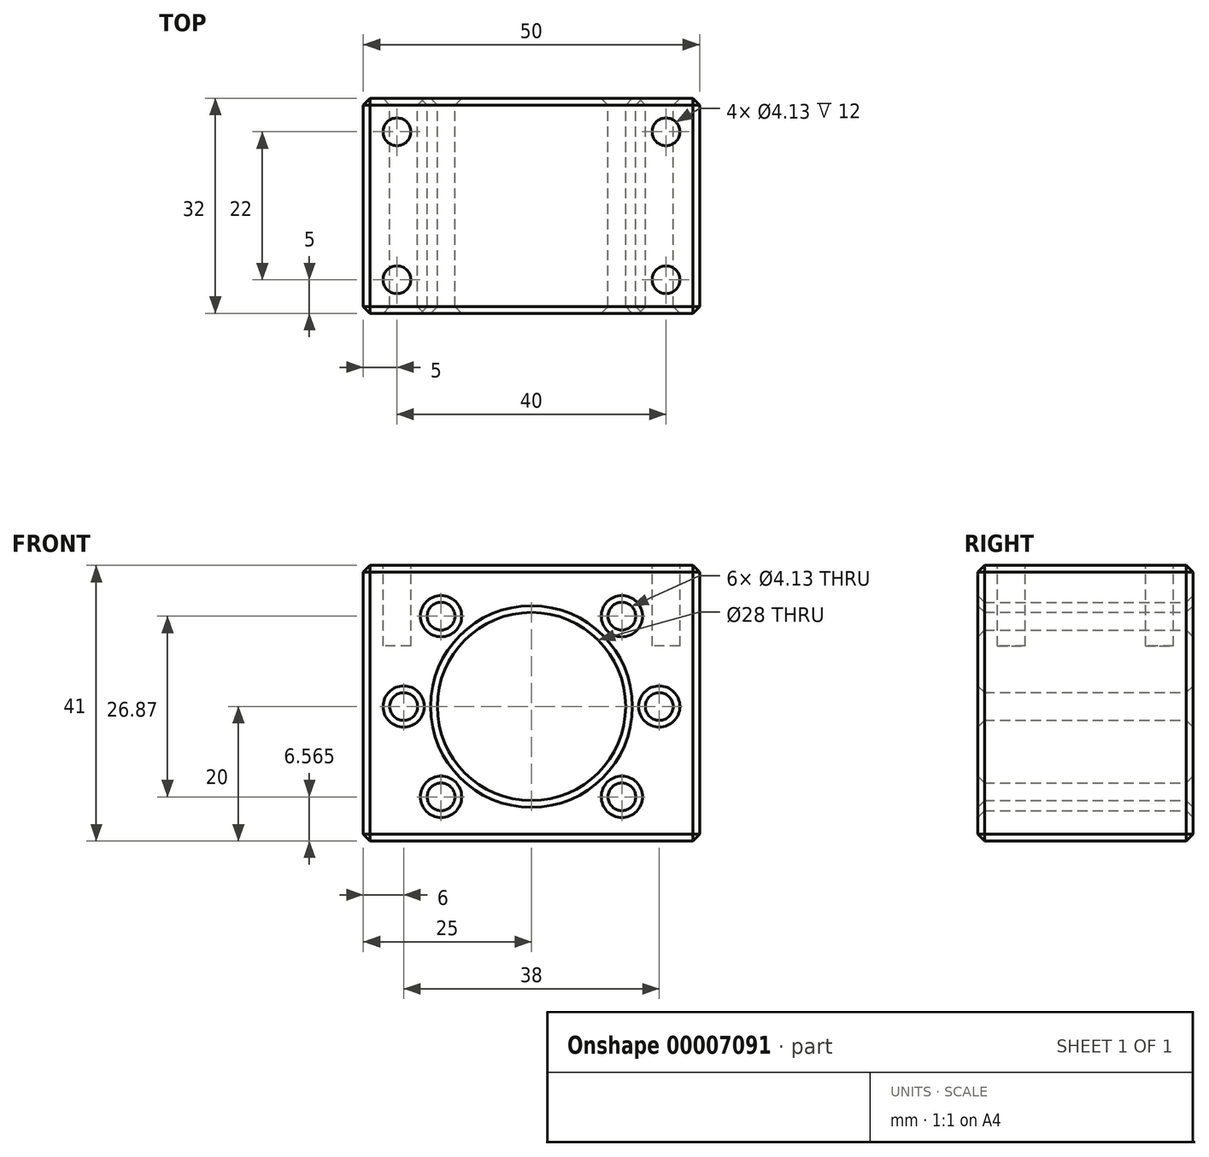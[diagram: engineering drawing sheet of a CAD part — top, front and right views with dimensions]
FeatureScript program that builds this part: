
annotation { "Feature Type Name" : "Feature", "Feature Type Description" : "" }
export const myFeature = defineFeature(function(context is Context, id is Id, definition is map)
    precondition{}
    {
        {
            var Q0;
            Q0=qCreatedBy(makeId("Front.planeOp"),FACE);
            var sketch = newSketch(context, id + "F0", { "sketchPlane" : qUnion([Q0])});
            skLineSegment(sketch, "E0.rect.bottom", {"start": v(25, -20) * mm, "end": v(-25, -20) * mm});
            skLineSegment(sketch, "E0.rect.top", {"start": v(25, 21) * mm, "end": v(-25, 21) * mm});
            skLineSegment(sketch, "E0.rect.left", {"start": v(25, -20) * mm, "end": v(25, 21) * mm});
            skLineSegment(sketch, "E0.rect.right", {"start": v(-25, -20) * mm, "end": v(-25, 21) * mm});
            skPoint(sketch, "E0.rect.middle", {"position": v(0, 0.5) * mm});
            skCircle(sketch, "E1", {"center": v(0, 0) * mm, "radius": 14 * mm});
            skCircle(sketch, "E2", {"center": v(-19, 0) * mm, "radius": 2.06 * mm});
            skCircle(sketch, "E3", {"center": v(0, 0) * mm, "radius": 19 * mm, "construction": true});
            skCircle(sketch, "E4", {"center": v(-13.44, 13.44) * mm, "radius": 2.06 * mm});
            skLineSegment(sketch, "E5", {"start": v(-13.44, 13.44) * mm, "end": v(0, 0) * mm, "construction": true});
            skCircle(sketch, "E6.0.MirrorC", {"center": v(-13.44, -13.44) * mm, "radius": 2.06 * mm});
            skCircle(sketch, "E7.0.MirrorC", {"center": v(13.44, 13.44) * mm, "radius": 2.06 * mm});
            skCircle(sketch, "E8.0.MirrorC", {"center": v(19, 0) * mm, "radius": 2.06 * mm});
            skCircle(sketch, "E9.0.MirrorC", {"center": v(13.44, -13.44) * mm, "radius": 2.06 * mm});
            skSolve(sketch);
        }
        {
            var Q0;
            Q0=makeQuery(id+"F0.imprint","IMPRINT",FACE,{"disambiguationData":[TD([[makeQuery(id+"F0.imprint","IMPRINT",EDGE,{"derivedFrom":sQuery(id+"F0.wireOp",EDGE,"E0.rect.bottom")}),-1.0]])]});
            extrude(context, id + "F1", {"entities" : qUnion([Q0]), "endBound" : BoundingType.SYMMETRIC, "depth" : 32 * mm});
        }
        {
            var Q0;
            Q0=makeQuery(id+"F1.opExtrude","SWEPT_FACE",FACE,{"disambiguationData":[OSD([sQuery(id+"F0.wireOp",EDGE,"E0.rect.top")])]});
            var sketch = newSketch(context, id + "F2", { "sketchPlane" : qUnion([Q0])});
            skCircle(sketch, "E10", {"center": v(-20, 11) * mm, "radius": 2.06 * mm});
            skCircle(sketch, "E11.0.MirrorC", {"center": v(-20, -11) * mm, "radius": 2.06 * mm});
            skCircle(sketch, "E12.0.MirrorC", {"center": v(20, 11) * mm, "radius": 2.06 * mm});
            skCircle(sketch, "E13.0.MirrorC", {"center": v(20, -11) * mm, "radius": 2.06 * mm});
            skSolve(sketch);
        }
        {
            var Q0;
            Q0 = qSketchRegion(id + "F2", true);
            extrude(context, id + "F3", {"entities" : qUnion([Q0]), "operationType" : NewBodyOperationType.REMOVE, "oppositeDirection" : true, "depth" : 12 * mm});
        }
        {
            var Q0;
            Q0=makeQuery(id+"F1.opExtrude","CAP_EDGE",EDGE,{"disambiguationData":[OSD([sQuery(id+"F0.wireOp",EDGE,"E8.0.MirrorC")])],"isStart":true});
            var Q1;
            Q1=makeQuery(id+"F1.opExtrude","CAP_EDGE",EDGE,{"disambiguationData":[OSD([sQuery(id+"F0.wireOp",EDGE,"E7.0.MirrorC")])],"isStart":true});
            var Q2;
            Q2=makeQuery(id+"F1.opExtrude","CAP_EDGE",EDGE,{"disambiguationData":[OSD([sQuery(id+"F0.wireOp",EDGE,"E4")])],"isStart":true});
            var Q3;
            Q3=makeQuery(id+"F1.opExtrude","CAP_EDGE",EDGE,{"disambiguationData":[OSD([sQuery(id+"F0.wireOp",EDGE,"E2")])],"isStart":true});
            var Q4;
            Q4=makeQuery(id+"F1.opExtrude","CAP_EDGE",EDGE,{"disambiguationData":[OSD([sQuery(id+"F0.wireOp",EDGE,"E6.0.MirrorC")])],"isStart":true});
            var Q5;
            Q5=makeQuery(id+"F1.opExtrude","CAP_EDGE",EDGE,{"disambiguationData":[OSD([sQuery(id+"F0.wireOp",EDGE,"E9.0.MirrorC")])],"isStart":true});
            var Q6;
            Q6=makeQuery(id+"F3.boolean.opBoolean","COPY",EDGE,{"derivedFrom":makeQuery(id+"F3.opExtrude","CAP_EDGE",EDGE,{"disambiguationData":[OSD([sQuery(id+"F2.wireOp",EDGE,"E12.0.MirrorC")])],"isStart":true})});
            var Q7;
            Q7=makeQuery(id+"F3.boolean.opBoolean","COPY",EDGE,{"derivedFrom":makeQuery(id+"F3.opExtrude","CAP_EDGE",EDGE,{"disambiguationData":[OSD([sQuery(id+"F2.wireOp",EDGE,"E13.0.MirrorC")])],"isStart":true})});
            var Q8;
            Q8=makeQuery(id+"F3.boolean.opBoolean","COPY",EDGE,{"derivedFrom":makeQuery(id+"F3.opExtrude","CAP_EDGE",EDGE,{"disambiguationData":[OSD([sQuery(id+"F2.wireOp",EDGE,"E11.0.MirrorC")])],"isStart":true})});
            var Q9;
            Q9=makeQuery(id+"F3.boolean.opBoolean","COPY",EDGE,{"derivedFrom":makeQuery(id+"F3.opExtrude","CAP_EDGE",EDGE,{"disambiguationData":[OSD([sQuery(id+"F2.wireOp",EDGE,"E10")])],"isStart":true})});
            var Q10;
            Q10=makeQuery(id+"F1.opExtrude","CAP_EDGE",EDGE,{"disambiguationData":[OSD([sQuery(id+"F0.wireOp",EDGE,"E7.0.MirrorC")])],"isStart":false});
            var Q11;
            Q11=makeQuery(id+"F1.opExtrude","CAP_EDGE",EDGE,{"disambiguationData":[OSD([sQuery(id+"F0.wireOp",EDGE,"E8.0.MirrorC")])],"isStart":false});
            var Q12;
            Q12=makeQuery(id+"F1.opExtrude","CAP_EDGE",EDGE,{"disambiguationData":[OSD([sQuery(id+"F0.wireOp",EDGE,"E9.0.MirrorC")])],"isStart":false});
            var Q13;
            Q13=makeQuery(id+"F1.opExtrude","CAP_EDGE",EDGE,{"disambiguationData":[OSD([sQuery(id+"F0.wireOp",EDGE,"E6.0.MirrorC")])],"isStart":false});
            var Q14;
            Q14=makeQuery(id+"F1.opExtrude","CAP_EDGE",EDGE,{"disambiguationData":[OSD([sQuery(id+"F0.wireOp",EDGE,"E2")])],"isStart":false});
            var Q15;
            Q15=makeQuery(id+"F1.opExtrude","CAP_EDGE",EDGE,{"disambiguationData":[OSD([sQuery(id+"F0.wireOp",EDGE,"E4")])],"isStart":false});
            var Q16;
            Q16=makeQuery(id+"F1.opExtrude","CAP_EDGE",EDGE,{"disambiguationData":[OSD([sQuery(id+"F0.wireOp",EDGE,"E1")])],"isStart":false});
            var Q17;
            Q17=makeQuery(id+"F1.opExtrude","CAP_EDGE",EDGE,{"disambiguationData":[OSD([sQuery(id+"F0.wireOp",EDGE,"E1")])],"isStart":true});
            chamfer(context, id + "F4", {"entities" : qUnion([Q0, Q1, Q2, Q3, Q4, Q5, Q6, Q7, Q8, Q9, Q10, Q11, Q12, Q13, Q14, Q15, Q16, Q17]), "width" : 1 * mm, "tangentPropagation" : true});
        }
        {
            var Q0;
            Q0=makeQuery(id+"F1.opExtrude","SWEPT_EDGE",EDGE,{"disambiguationData":[OSD([sQuery(id+"F0.wireOp",EDGE,"E0.rect.bottom"),sQuery(id+"F0.wireOp",EDGE,"E0.rect.right")])]});
            var Q1;
            Q1=makeQuery(id+"F1.opExtrude","CAP_EDGE",EDGE,{"disambiguationData":[OSD([sQuery(id+"F0.wireOp",EDGE,"E0.rect.bottom")])],"isStart":true});
            var Q2;
            Q2=makeQuery(id+"F1.opExtrude","CAP_EDGE",EDGE,{"disambiguationData":[OSD([sQuery(id+"F0.wireOp",EDGE,"E0.rect.bottom")])],"isStart":false});
            var Q3;
            Q3=makeQuery(id+"F1.opExtrude","CAP_EDGE",EDGE,{"disambiguationData":[OSD([sQuery(id+"F0.wireOp",EDGE,"E0.rect.right")])],"isStart":true});
            var Q4;
            Q4=makeQuery(id+"F1.opExtrude","CAP_EDGE",EDGE,{"disambiguationData":[OSD([sQuery(id+"F0.wireOp",EDGE,"E0.rect.top")])],"isStart":true});
            var Q5;
            Q5=makeQuery(id+"F1.opExtrude","SWEPT_EDGE",EDGE,{"disambiguationData":[OSD([sQuery(id+"F0.wireOp",EDGE,"E0.rect.top"),sQuery(id+"F0.wireOp",EDGE,"E0.rect.right")])]});
            var Q6;
            Q6=makeQuery(id+"F1.opExtrude","CAP_EDGE",EDGE,{"disambiguationData":[OSD([sQuery(id+"F0.wireOp",EDGE,"E0.rect.right")])],"isStart":false});
            var Q7;
            Q7=makeQuery(id+"F1.opExtrude","CAP_EDGE",EDGE,{"disambiguationData":[OSD([sQuery(id+"F0.wireOp",EDGE,"E0.rect.left")])],"isStart":false});
            var Q8;
            Q8=makeQuery(id+"F1.opExtrude","CAP_EDGE",EDGE,{"disambiguationData":[OSD([sQuery(id+"F0.wireOp",EDGE,"E0.rect.top")])],"isStart":false});
            var Q9;
            Q9=makeQuery(id+"F1.opExtrude","SWEPT_EDGE",EDGE,{"disambiguationData":[OSD([sQuery(id+"F0.wireOp",EDGE,"E0.rect.top"),sQuery(id+"F0.wireOp",EDGE,"E0.rect.left")])]});
            var Q10;
            Q10=makeQuery(id+"F1.opExtrude","SWEPT_EDGE",EDGE,{"disambiguationData":[OSD([sQuery(id+"F0.wireOp",EDGE,"E0.rect.bottom"),sQuery(id+"F0.wireOp",EDGE,"E0.rect.left")])]});
            var Q11;
            Q11=makeQuery(id+"F1.opExtrude","CAP_EDGE",EDGE,{"disambiguationData":[OSD([sQuery(id+"F0.wireOp",EDGE,"E0.rect.left")])],"isStart":true});
            chamfer(context, id + "F5", {"entities" : qUnion([Q0, Q1, Q2, Q3, Q4, Q5, Q6, Q7, Q8, Q9, Q10, Q11]), "width" : 1 * mm, "tangentPropagation" : true});
        }
    });
